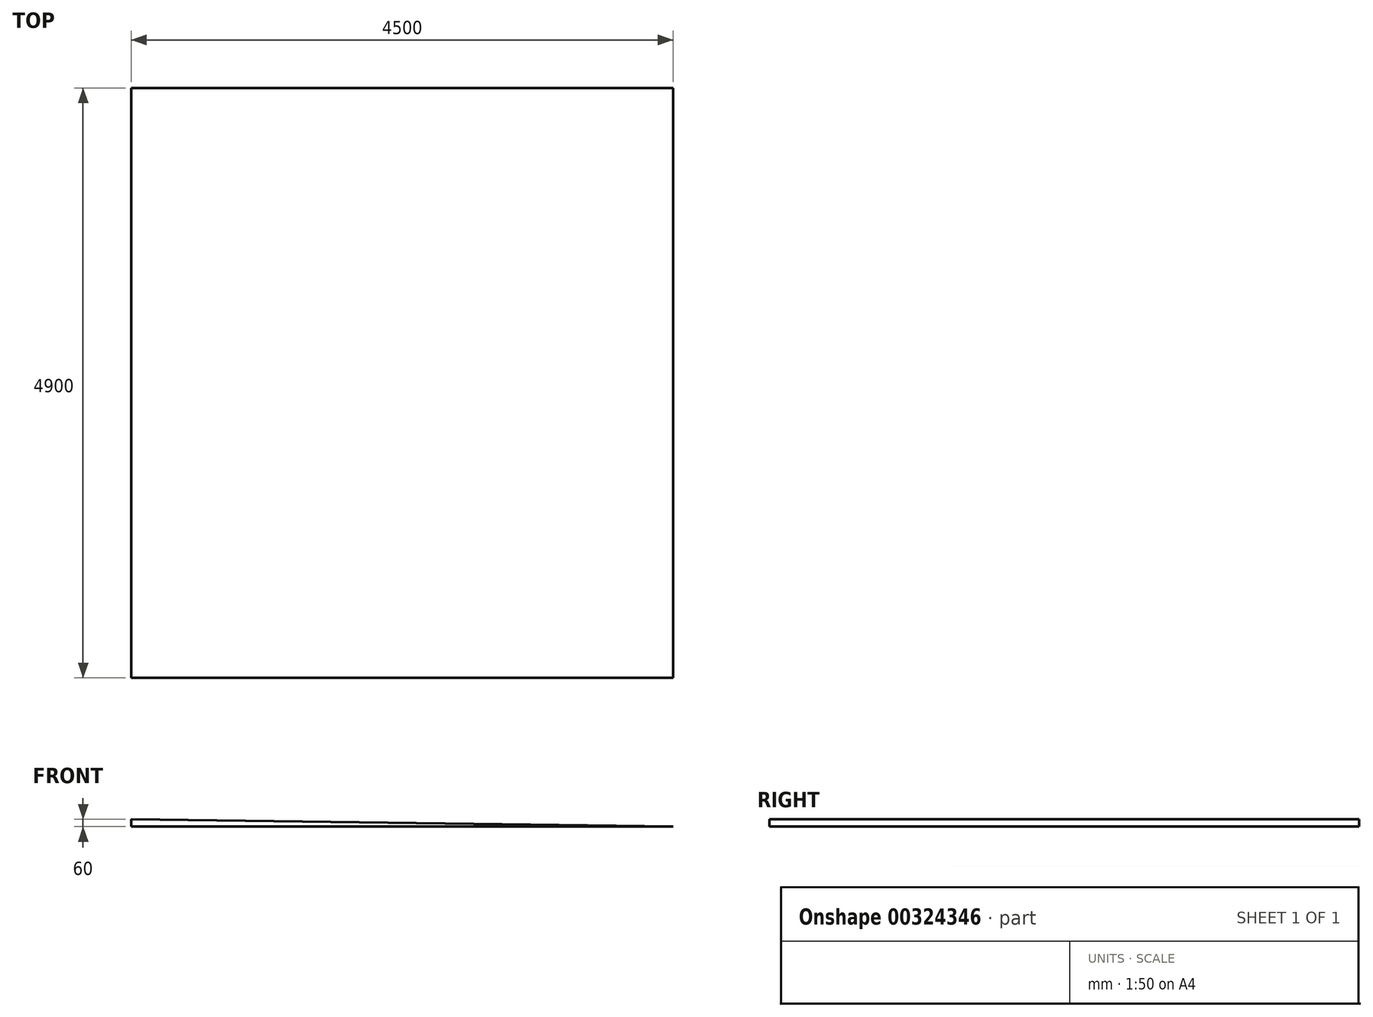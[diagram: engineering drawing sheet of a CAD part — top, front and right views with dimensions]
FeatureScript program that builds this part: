
annotation { "Feature Type Name" : "Feature", "Feature Type Description" : "" }
export const myFeature = defineFeature(function(context is Context, id is Id, definition is map)
    precondition{}
    {
        {
            var Q0;
            Q0=qCreatedBy(makeId("Front.planeOp"),FACE);
            var sketch = newSketch(context, id + "F0", { "sketchPlane" : qUnion([Q0])});
            skLineSegment(sketch, "E0", {"start": v(4357.1, 0) * mm, "end": v(-142.9, 0) * mm});
            skLineSegment(sketch, "E1", {"start": v(-142.9, 0) * mm, "end": v(-142.9, 60) * mm});
            skLineSegment(sketch, "E2", {"start": v(-142.9, 60) * mm, "end": v(4357.1, 0) * mm});
            skLineSegment(sketch, "E3", {"start": v(4357.1, 0) * mm, "end": v(4357.1, 0) * mm});
            skSolve(sketch);
        }
        {
            var Q0;
            Q0=makeQuery(id+"F0.imprint","IMPRINT",FACE,{"disambiguationData":[TD([[makeQuery(id+"F0.imprint","IMPRINT",EDGE,{"derivedFrom":sQuery(id+"F0.wireOp",EDGE,"E0")}),-1.0]])]});
            extrude(context, id + "F1", {"entities" : qUnion([Q0]), "depth" : 4900 * mm});
        }
    });
